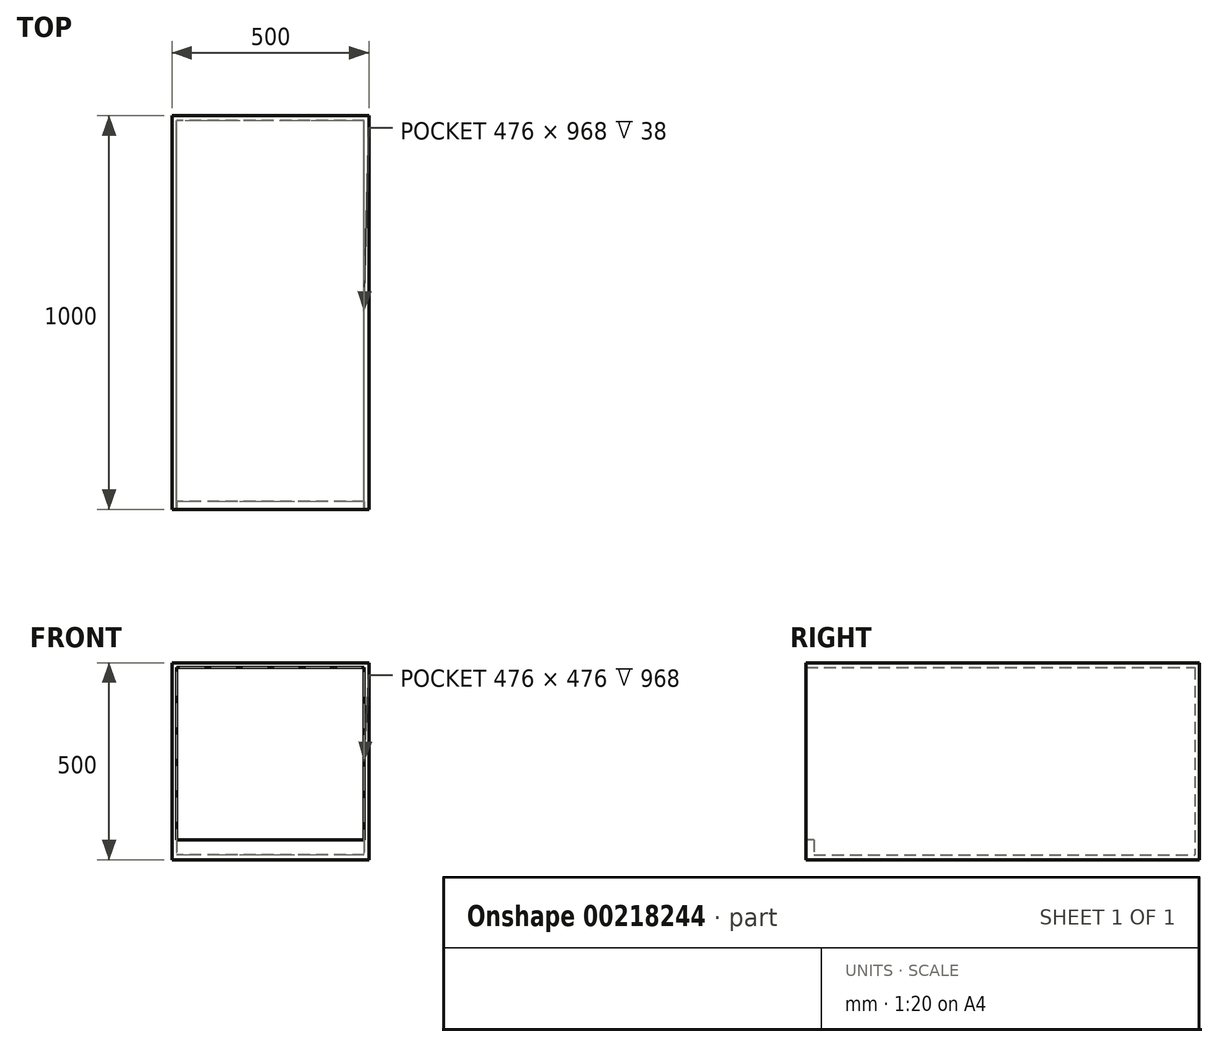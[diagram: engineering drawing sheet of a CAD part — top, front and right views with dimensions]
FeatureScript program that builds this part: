
annotation { "Feature Type Name" : "Feature", "Feature Type Description" : "" }
export const myFeature = defineFeature(function(context is Context, id is Id, definition is map)
    precondition{}
    {
        {
            var Q0;
            Q0=qCreatedBy(makeId("Top.planeOp"),FACE);
            var sketch = newSketch(context, id + "F0", { "sketchPlane" : qUnion([Q0])});
            skLineSegment(sketch, "E0.bottom", {"start": v(250, -500) * mm, "end": v(-250, -500) * mm});
            skLineSegment(sketch, "E0.top", {"start": v(250, 500) * mm, "end": v(-250, 500) * mm});
            skLineSegment(sketch, "E0.left", {"start": v(250, -500) * mm, "end": v(250, 500) * mm});
            skLineSegment(sketch, "E0.right", {"start": v(-250, -500) * mm, "end": v(-250, 500) * mm});
            skPoint(sketch, "E0.middle", {"position": v(0, 0) * mm});
            skSolve(sketch);
        }
        {
            var Q0;
            Q0=makeQuery(id+"F0.imprint","IMPRINT",FACE,{"disambiguationData":[TD([[makeQuery(id+"F0.imprint","IMPRINT",EDGE,{"derivedFrom":sQuery(id+"F0.wireOp",EDGE,"E0.bottom")}),-1.0]])]});
            extrude(context, id + "F1", {"entities" : qUnion([Q0]), "depth" : 500 * mm});
        }
        {
            var Q0;
            Q0=makeQuery(id+"F1.opExtrude","SWEPT_FACE",FACE,{"disambiguationData":[OSD([sQuery(id+"F0.wireOp",EDGE,"E0.bottom")])]});
            shell(context, id + "F2", {"entities" : qUnion([Q0]), "thickness" : 12 * mm});
        }
        {
            var Q0;
            Q0=makeQuery(id+"F1.opExtrude","SWEPT_FACE",FACE,{"disambiguationData":[OSD([sQuery(id+"F0.wireOp",EDGE,"E0.bottom")])]});
            var sketch = newSketch(context, id + "F3", { "sketchPlane" : qUnion([Q0])});
            skLineSegment(sketch, "E1", {"start": v(-238, 50) * mm, "end": v(238, 50) * mm});
            skSolve(sketch);
        }
        {
            var Q0;
            {var subQ0=sQuery(id+"F3.wireOp",EDGE,"E1");Q0=makeQuery(id+"F3.imprint","IMPRINT",FACE,{"disambiguationData":[TD([[makeQuery(id+"F3.imprint","IMPRINT",EDGE,{"derivedFrom":subQ0}),-1.0]])]});}
            extrude(context, id + "F4", {"entities" : qUnion([Q0]), "operationType" : NewBodyOperationType.ADD, "oppositeDirection" : true, "depth" : 20 * mm});
        }
    });
